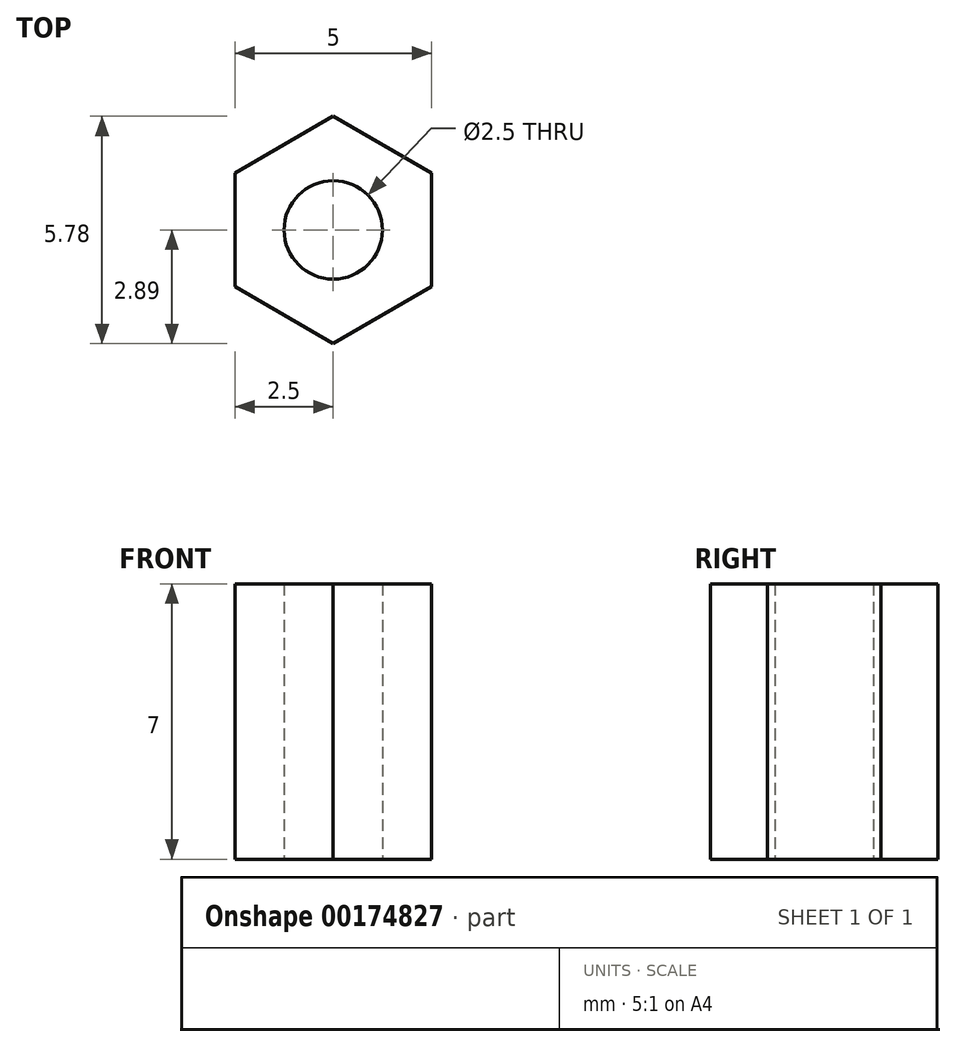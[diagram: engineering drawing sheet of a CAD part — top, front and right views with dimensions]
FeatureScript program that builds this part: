
annotation { "Feature Type Name" : "Feature", "Feature Type Description" : "" }
export const myFeature = defineFeature(function(context is Context, id is Id, definition is map)
    precondition{}
    {
        {
            var Q0;
            Q0=qCreatedBy(makeId("Top.planeOp"),FACE);
            var sketch = newSketch(context, id + "F0", { "sketchPlane" : qUnion([Q0])});
            skCircle(sketch, "E0.cCircle", {"center": v(0, 0) * mm, "radius": 2.5 * mm, "construction": true});
            skLineSegment(sketch, "E0.0", {"start": v(2.5, -1.44) * mm, "end": v(0, -2.89) * mm});
            skLineSegment(sketch, "E0.1", {"start": v(0, -2.89) * mm, "end": v(-2.5, -1.44) * mm});
            skLineSegment(sketch, "E0.2", {"start": v(-2.5, -1.44) * mm, "end": v(-2.5, 1.44) * mm});
            skLineSegment(sketch, "E0.3", {"start": v(-2.5, 1.44) * mm, "end": v(0, 2.89) * mm});
            skLineSegment(sketch, "E0.4", {"start": v(0, 2.89) * mm, "end": v(2.5, 1.44) * mm});
            skLineSegment(sketch, "E0.5", {"start": v(2.5, 1.44) * mm, "end": v(2.5, -1.44) * mm});
            skPoint(sketch, "E0.0.midPoint", {"position": v(1.25, -2.17) * mm});
            skCircle(sketch, "E1", {"center": v(0, 0) * mm, "radius": 1.25 * mm});
            skSolve(sketch);
        }
        {
            var Q0;
            Q0=qSketchRegion(id+"F0",true);
            extrude(context, id + "F1", {"entities" : qUnion([Q0]), "depth" : 7 * mm});
        }
    });
